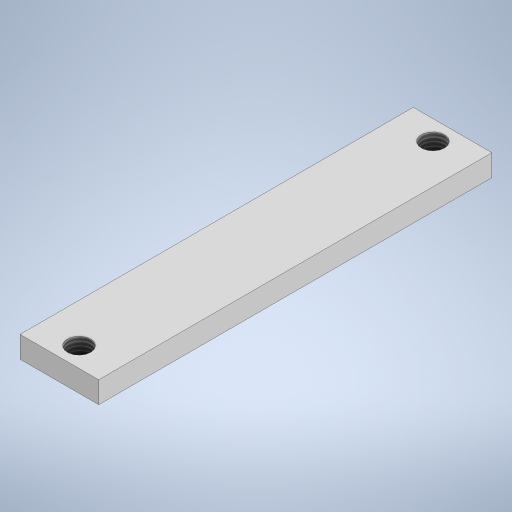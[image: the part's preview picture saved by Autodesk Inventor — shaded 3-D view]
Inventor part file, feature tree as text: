
AUTODESK INVENTOR PART (.ipt)
format: ipt  version: 2023 (Build 270158000, 158)  size: 227,328 bytes
history: native  units: mm
features: sketch x1, extrude x1, hole x1
ambient origin geometry x8: Origin, YZ Plane, XZ Plane, XY Plane, X Axis, Y Axis, Z Axis, Center Point
bodies: Solid1 (feature_tree)
feature tree (3):
  sketch  "Sketch1"  dims[d0=100.0mm d1=20.0mm d2=90.0mm d3=5.0mm d4=5.5mm d5=0.0mm d6=5.917468mm d7=14.0mm d8=4.0mm d9=2.0mm d10=90.0deg d11=19.1mm d12=20.594885mm]
  extrude  "Extrusion1"  Depth=20.0mm
  hole  "Hole1"  [1 undecoded]
note: 1 required parameter value undecoded (feature->parameter linkage not recoverable at this tier; creation-order binding heuristic only, values carry confidence <= 0.55)
